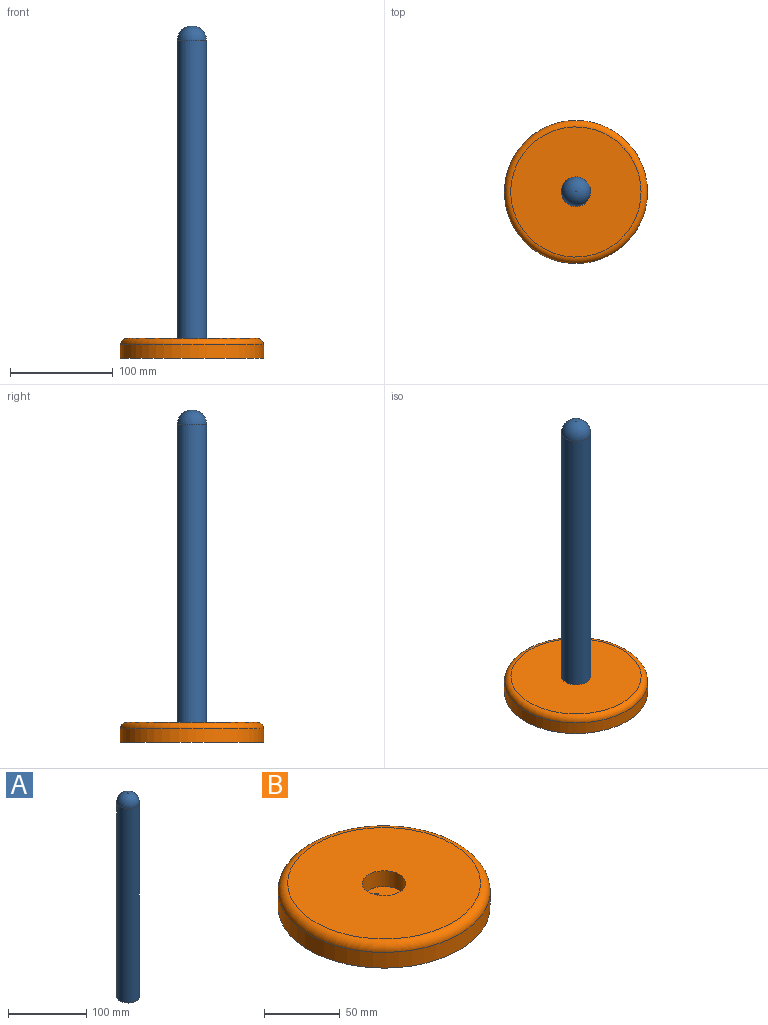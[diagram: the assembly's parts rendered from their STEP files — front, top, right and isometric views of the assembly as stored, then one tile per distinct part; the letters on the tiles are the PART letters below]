
ASSEMBLY  parts=2 mates=1
PART A: 4 faces, bbox 28.5x28.5x317.5 mm
  f0: plane 0.56x0.56mm, normal (0,0,1), area 0.2mm2, adj f1
  f1: torus R=0.28mm, axis (0,0,1), area 1264.8mm2, adj f0
  f2: cylinder r=14.25mm len=303.53mm, axis (0,0,-1), area 27176.7mm2, adj f3
  f3: plane 28.5x28.5mm, normal (0,0,-1), area 637.9mm2, adj f2
PART B: 8 faces, bbox 151.2x151.2x19.1 mm
  f0: cylinder r=14.25mm len=28.5mm, axis (0,0,-1), area 1137.1mm2, adj f2,f6
  f1: cylinder r=69.85mm len=139.7mm, axis (0,0,-1), area 5573.8mm2, adj f3,f7
  f2: plane 127x127mm, normal (0,0,1), area 12029.7mm2, adj f0,f7
  f3: plane 139.7x139.7mm, normal (0,0,-1), area 15312.1mm2, adj f1,f4,f5
  f4: cylinder r=1.59mm len=6.35mm, axis (0,0,-1), area 63.3mm2, adj f3,f6
  f5: cylinder r=1.59mm len=6.35mm, axis (0,0,-1), area 63.3mm2, adj f3,f6
  f6: plane 28.5x28.5mm, normal (0,0,1), area 622.1mm2, adj f0,f4,f5
  f7: torus R=63.5mm, axis (0,0,1), area 4233mm2, adj f1,f2
PLACE A t=(26.19,21.55,20.01)mm
PLACE B t=(-34.41,-44.66,13.66)mm
MATE fastened A.f1 <-> B.f0  axis (0,0,-1) through (57.54,48.68,20.01)mm
